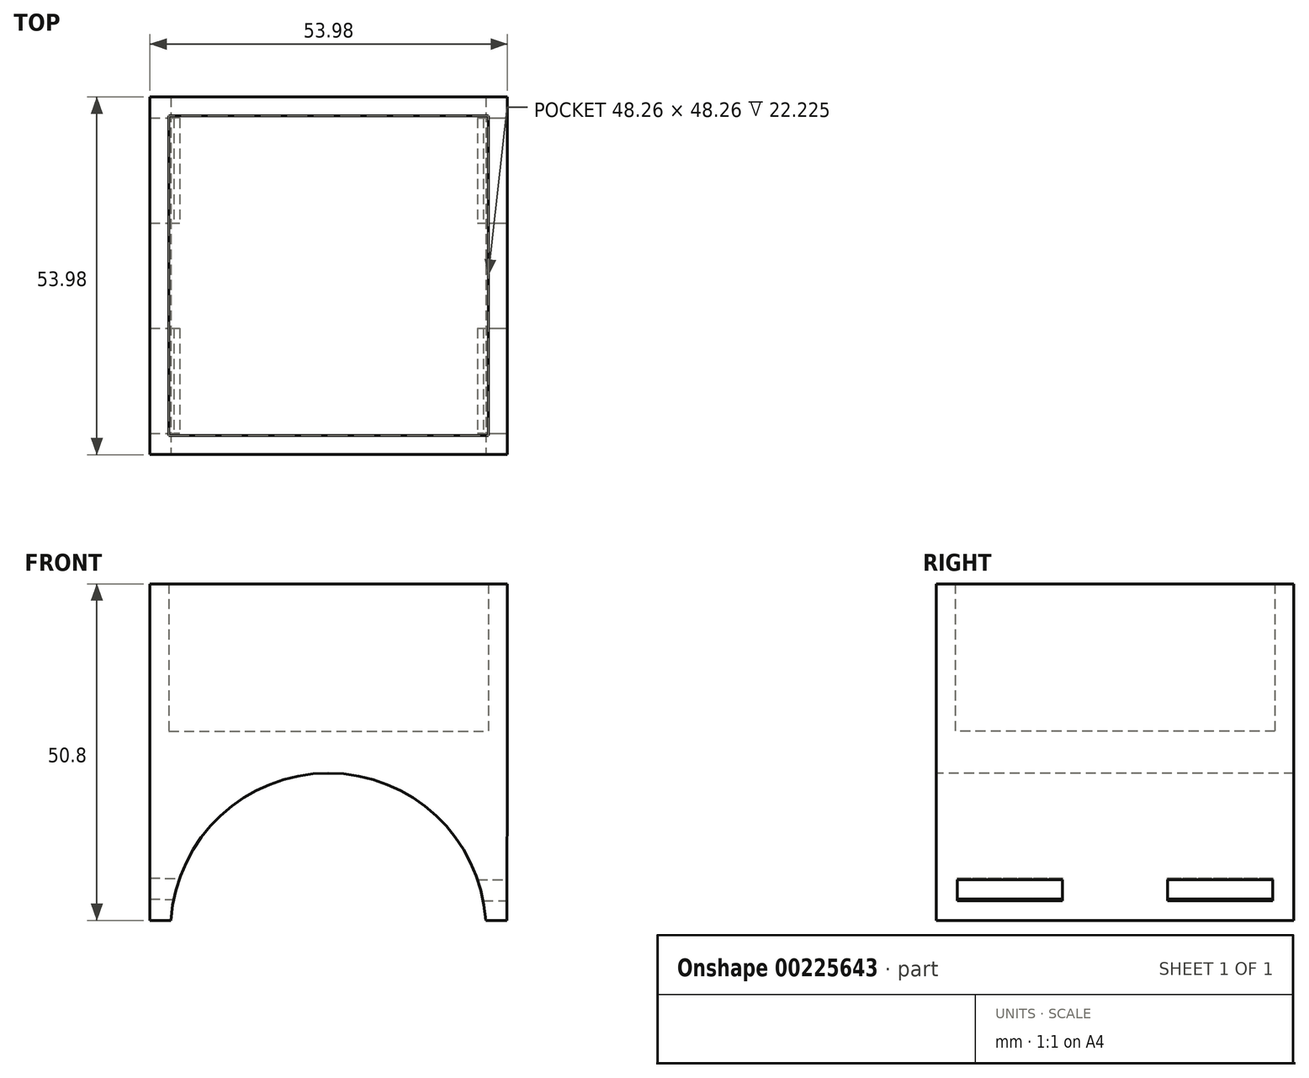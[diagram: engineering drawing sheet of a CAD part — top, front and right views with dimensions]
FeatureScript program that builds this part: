
annotation { "Feature Type Name" : "Feature", "Feature Type Description" : "" }
export const myFeature = defineFeature(function(context is Context, id is Id, definition is map)
    precondition{}
    {
        {
            var Q0;
            Q0=qCreatedBy(makeId("Top.planeOp"),FACE);
            var sketch = newSketch(context, id + "F0", { "sketchPlane" : qUnion([Q0])});
            skLineSegment(sketch, "E0.bottom", {"start": v(-24.13, 24.13) * mm, "end": v(24.13, 24.13) * mm});
            skLineSegment(sketch, "E0.top", {"start": v(-24.13, -24.13) * mm, "end": v(24.13, -24.13) * mm});
            skLineSegment(sketch, "E0.left", {"start": v(-24.13, 24.13) * mm, "end": v(-24.13, -24.13) * mm});
            skLineSegment(sketch, "E0.right", {"start": v(24.13, 24.13) * mm, "end": v(24.13, -24.13) * mm});
            skPoint(sketch, "E0.middle", {"position": v(0, 0) * mm});
            skLineSegment(sketch, "E1.bottom", {"start": v(26.99, 26.99) * mm, "end": v(-26.99, 26.99) * mm});
            skLineSegment(sketch, "E1.top", {"start": v(26.99, -26.99) * mm, "end": v(-26.99, -26.99) * mm});
            skLineSegment(sketch, "E1.left", {"start": v(26.99, 26.99) * mm, "end": v(26.99, -26.99) * mm});
            skLineSegment(sketch, "E1.right", {"start": v(-26.99, 26.99) * mm, "end": v(-26.99, -26.99) * mm});
            skSolve(sketch);
        }
        {
            var Q0;
            Q0=makeQuery(id+"F0.imprint","IMPRINT",FACE,{"disambiguationData":[TD([[makeQuery(id+"F0.imprint","IMPRINT",EDGE,{"derivedFrom":sQuery(id+"F0.wireOp",EDGE,"E0.bottom")}),-1.0]])]});
            extrude(context, id + "F1", {"entities" : qUnion([Q0]), "depth" : 3.17 * mm});
        }
        {
            var Q0;
            Q0=makeQuery(id+"F0.imprint","IMPRINT",FACE,{"disambiguationData":[TD([[makeQuery(id+"F0.imprint","IMPRINT",EDGE,{"derivedFrom":sQuery(id+"F0.wireOp",EDGE,"E0.bottom")}),1.0]])]});
            extrude(context, id + "F2", {"entities" : qUnion([Q0]), "operationType" : NewBodyOperationType.ADD, "depth" : 25.4 * mm});
        }
        {
            var Q0;
            Q0=makeQuery(id+"FyGfKlmvclPCMsU_1.boolean.opBoolean","MERGE",FACE,{"derivedFrom":[makeQuery(id+"F2.opExtrude","SWEPT_FACE",FACE,{"disambiguationData":[OSD([sQuery(id+"F0.wireOp",EDGE,"E1.top")])]}),makeQuery(id+"FyGfKlmvclPCMsU_1.opExtrude","CAP_FACE",FACE,{"disambiguationData":[OSD([sQuery(id+"Fhr7sJcQjuV9vg2_1.wireOp",EDGE,"op8FXRoq-AiBK-wzXs-gnUn-wm1Rc7jBiXtZ.bottom"),sQuery(id+"Fhr7sJcQjuV9vg2_1.wireOp",EDGE,"op8FXRoq-AiBK-wzXs-gnUn-wm1Rc7jBiXtZ.top"),sQuery(id+"Fhr7sJcQjuV9vg2_1.wireOp",EDGE,"op8FXRoq-AiBK-wzXs-gnUn-wm1Rc7jBiXtZ.left"),sQuery(id+"Fhr7sJcQjuV9vg2_1.wireOp",EDGE,"op8FXRoq-AiBK-wzXs-gnUn-wm1Rc7jBiXtZ.right"),sQuery(id+"Fhr7sJcQjuV9vg2_1.wireOp",EDGE,"8VTqBtl9-Z2f6-vGyF-VyAn-BKKNYNf7U0EH.top"),sQuery(id+"Fhr7sJcQjuV9vg2_1.wireOp",EDGE,"8VTqBtl9-Z2f6-vGyF-VyAn-BKKNYNf7U0EH.left"),sQuery(id+"Fhr7sJcQjuV9vg2_1.wireOp",EDGE,"8VTqBtl9-Z2f6-vGyF-VyAn-BKKNYNf7U0EH.right")])],"isStart":true}),makeQuery(id+"FyGfKlmvclPCMsU_1.opExtrude","CAP_FACE",FACE,{"disambiguationData":[OSD([sQuery(id+"Fhr7sJcQjuV9vg2_1.wireOp",EDGE,"fe899fc1-eba9-4522-8600-3ce30c8c48550.MirrorCS"),sQuery(id+"Fhr7sJcQjuV9vg2_1.wireOp",EDGE,"7b314edd-bf01-442e-a387-1c7213c7432e0.MirrorCS"),sQuery(id+"Fhr7sJcQjuV9vg2_1.wireOp",EDGE,"f0e91ec7-8962-4b76-a96e-a30abec756c50.MirrorCS"),sQuery(id+"Fhr7sJcQjuV9vg2_1.wireOp",EDGE,"07d9bbe1-430e-41e6-b703-f5f7d67f3e6d0.MirrorCS"),sQuery(id+"Fhr7sJcQjuV9vg2_1.wireOp",EDGE,"f779dba9-1e03-481e-84c7-e8e494c02fc80.MirrorCS"),sQuery(id+"Fhr7sJcQjuV9vg2_1.wireOp",EDGE,"bbd5e38c-de79-4c04-ae09-a65da71bd5440.MirrorCS"),sQuery(id+"Fhr7sJcQjuV9vg2_1.wireOp",EDGE,"52e1bf0f-c555-4af5-8906-2e17a938ddec0.MirrorCS")])],"isStart":true})]});
            var sketch = newSketch(context, id + "F3", { "sketchPlane" : qUnion([Q0])});
            skLineSegment(sketch, "E2", {"start": v(-26.99, 0) * mm, "end": v(-26.99, -25.4) * mm});
            skPoint(sketch, "E2.endSnap0", {"position": v(-26.99, 12.7) * mm});
            skLineSegment(sketch, "E3.bottom", {"start": v(-26.99, -25.4) * mm, "end": v(26.88, -25.4) * mm});
            skLineSegment(sketch, "E3.top", {"start": v(-26.99, 0) * mm, "end": v(26.99, 0) * mm});
            skLineSegment(sketch, "E3.right", {"start": v(26.88, -25.4) * mm, "end": v(26.99, 0) * mm});
            skPoint(sketch, "E4", {"position": v(-23.81, -25.4) * mm});
            skPoint(sketch, "E5", {"position": v(23.7, -25.4) * mm});
            skArc(sketch, "E6", {"start": v(23.7, -25.4) * mm, "mid": v(-0.05, -3.18) * mm, "end": v(-23.81, -25.4) * mm});
            skSolve(sketch);
        }
        {
            var Q0;
            {var subQ3=sQuery(id+"F3.wireOp",EDGE,"E2");Q0=makeQuery(id+"F3.imprint","IMPRINT",FACE,{"disambiguationData":[TD([[makeQuery(id+"F3.imprint","IMPRINT",EDGE,{"derivedFrom":subQ3}),1.0]])]});}
            extrude(context, id + "F4", {"entities" : qUnion([Q0]), "operationType" : NewBodyOperationType.ADD, "oppositeDirection" : true, "depth" : 53.97 * mm});
        }
        {
            var Q0;
            Q0=makeQuery(id+"F4.opExtrude","SWEPT_FACE",FACE,{"disambiguationData":[OSD([sQuery(id+"F3.wireOp",EDGE,"E3.right")])]});
            var sketch = newSketch(context, id + "F5", { "sketchPlane" : qUnion([Q0])});
            skLineSegment(sketch, "E7.bottom", {"start": v(-23.81, -2.65) * mm, "end": v(23.81, -2.65) * mm});
            skLineSegment(sketch, "E7.top", {"start": v(-23.81, -22.32) * mm, "end": v(23.81, -22.32) * mm});
            skLineSegment(sketch, "E7.left", {"start": v(-23.81, -2.65) * mm, "end": v(-23.81, -22.32) * mm});
            skLineSegment(sketch, "E7.right", {"start": v(23.81, -2.65) * mm, "end": v(23.81, -22.32) * mm});
            skPoint(sketch, "E7.middle", {"position": v(0, -12.49) * mm});
            skLineSegment(sketch, "E8.bottom", {"start": v(-23.81, -19.15) * mm, "end": v(23.81, -19.15) * mm});
            skLineSegment(sketch, "E8.top", {"start": v(-23.81, -5.82) * mm, "end": v(23.81, -5.82) * mm});
            skLineSegment(sketch, "E8.left", {"start": v(-23.81, -19.15) * mm, "end": v(-23.81, -5.82) * mm});
            skLineSegment(sketch, "E8.right", {"start": v(23.81, -19.15) * mm, "end": v(23.81, -5.82) * mm});
            skLineSegment(sketch, "E9.bottom", {"start": v(-7.94, -22.32) * mm, "end": v(7.94, -22.32) * mm});
            skLineSegment(sketch, "E9.top", {"start": v(-7.94, -15.97) * mm, "end": v(7.94, -15.97) * mm});
            skLineSegment(sketch, "E9.left", {"start": v(-7.94, -22.32) * mm, "end": v(-7.94, -15.97) * mm});
            skLineSegment(sketch, "E9.right", {"start": v(7.94, -22.32) * mm, "end": v(7.94, -15.97) * mm});
            skPoint(sketch, "E9.middle", {"position": v(0, -19.15) * mm});
            skSolve(sketch);
        }
        {
            var Q0;
            {var subQ0=sQuery(id+"F5.wireOp",EDGE,"E7.left");var subQ1=sQuery(id+"F5.wireOp",EDGE,"E7.top");var subQ2=makeQuery(id+"F5.imprint","INTERSECT",VERTEX,{"derivedFrom":[subQ1,subQ0]});Q0=makeQuery(id+"F5.imprint","IMPRINT",FACE,{"disambiguationData":[TD([[makeQuery(id+"F5.imprint","IMPRINT",EDGE,{"disambiguationData":[TD([[subQ2,-1.0]])],"derivedFrom":subQ1}),1.0]])]});}
            var Q1;
            {var subQ0=sQuery(id+"F5.wireOp",EDGE,"E7.right");var subQ1=sQuery(id+"F5.wireOp",EDGE,"E7.top");var subQ2=makeQuery(id+"F5.imprint","INTERSECT",VERTEX,{"derivedFrom":[subQ1,subQ0]});Q1=makeQuery(id+"F5.imprint","IMPRINT",FACE,{"disambiguationData":[TD([[makeQuery(id+"F5.imprint","IMPRINT",EDGE,{"disambiguationData":[TD([[subQ2,1.0]])],"derivedFrom":subQ1}),1.0]])]});}
            extrude(context, id + "F6", {"entities" : qUnion([Q0, Q1]), "operationType" : NewBodyOperationType.REMOVE, "oppositeDirection" : true, "depth" : 63.5 * mm});
        }
    });
